# Revit family: VIESSMANN - Vitocal 300-G Pro
name_source: partatom
category: Wyposażenie mechaniczne
revit_build: Autodesk Revit 2017 (Build: 20160720_1515(x64)
units: mm (PartAtom-declared; Revit-internal decimal feet)

## family parameters
Numer OmniClass = 23.75.10.21.17
Oparty na płaszczyźnie roboczej = Nie
Punkt obliczania pomieszczeń = Nie
Tnij formami wycięć po wczytaniu = Nie
Typ części = Normalny
Tytuł OmniClass = Water-Source Heat Pumps
Współdzielony = Nie
Wymiar okrągłego złącza = Użyj średnicy
Zawsze pionowo = Tak

## types (5) — shared parameters
Autor = www.archispace.pl
Czynnik chłodniczy = R410A
Częstotliwość = 50 Hz
Dopuszczalne ciśnienie robocze. Strona niskociśnieniowa = 1.8 MPa
Dopuszczalne ciśnienie robocze. Strona wysokociśnieniowa = 4.5 MPa
Liczba biegunów = 3
Liczba obiegów chłodniczych = 1
Liczba sprężarek = 2
Model = Solankowa pompa ciepła Vitocal 300-G PRO 80kW / Brine-water heat pump Vitocal 300-G PRO 80kW
Napięcie znamionowe = 400 V
Obieg pierwotny od strony parownika (Victaulic) = 3" (DN 80)
Obieg pierwotny od strony zestawu przyłączy (kołnierz) = DN 80/PN 10
Obieg pierwotny. Ochrona przed zamarzaniem/temperatura początku krystalizacji (zalecany czynnik chłodzący Tyfocor) = -16 °C
Obieg pierwotny. Różnica temperatur = 3 °C
Obieg wtórny od strony skraplacza (Victaulic) = 2½" (DN 65)
Obieg wtórny od strony zestawu przyłączy (kołnierz) = DN 65/PN 10
Obieg wtórny. Maks. temperatura na zasilaniu na wlocie z obiegu pierwotnego B +5°C = 60 °C
Obieg wtórny. Maks. temperatura na zasilaniu na wlocie z obiegu pierwotnego B 0°C = 55 °C
Obieg wtórny. Różnica temperatur = 5 °C
Opis = Pompy ciepła z napędem elektrycznym do ogrzewania i podgrzewu ciepłej wody użytkowej w jedno- lub dwusystemowych instalacjach grzewczych.
Podłączenie A odsunięcie = 271 mm  [stored 0.889108 ft]
Podłączenie A wysokość = 1139 mm  [stored 3.73688 ft]
Podłączenie B odsunięcie = 300 mm  [stored 0.984252 ft]
Podłączenie B wysokość = 1169 mm  [stored 3.8353 ft]
Podłączenie C odsunięcie = 271 mm  [stored 0.889108 ft]
Podłączenie C wysokość = 609 mm  [stored 1.99803 ft]
Podłączenie D odsunięcie = 300 mm  [stored 0.984252 ft]
Podłączenie D wysokość = 639 mm  [stored 2.09646 ft]
Producent = Viessmann Sp. z o.o.
Regulator. Bezpiecznik = T6,3AH/250 V
Regulator. Klasa ochrony/stopnień ochrony = IP20
Regulator. Maks. pobór mocy elektrycznej 1. i 2. stopnia = 45 W
Regulator. Maks. pobór mocy elektrycznej 1. stopnia = 25 W
Regulator. Maks. pobór mocy elektrycznej 2. stopnia = 20 W
Regulator. Moc znamionowa = 1000 W
Regulator. Napięcie znamionowe = 1/N/PE 230 V/50 Hz
Regulator. Zabezpieczenie (wewnętrzne) = 1 x B16A
Rodzaj sprężarki = Scroll - całkowicie hermetyczna
Stopień ochrony = IP20
System rozruchowy = Moduł łagodnego rozruchu
Szerokość całkowita = 911 mm  [stored 2.98885 ft]
Szerokość przy wstawianiu bez osłon bocznych = 850 mm  [stored 2.78871 ft]
URL = https://www.viessmann-projektant.pl
Viessmann Kolor 1 = Viessmann Kolor 1
Wysokość całkowita = 1650 mm  [stored 5.41339 ft]
Zasilanie elektryczne (V/ph/Hz) = 3LNPE/400 V/50 Hz
Średnica odejścia 1 = 80 mm  [stored 0.262467 ft]
Średnica odejścia 2 = 65 mm  [stored 0.213255 ft]

## per-type parameters (varying)
- BW 302.D090. Solanka/woda (B0/W35): Całkowity maksymalny pobór mocy=48.0 kW; Całkowity prąd rozruchowy=145 A; Cos Phi sprężarki przy maks. mocy w B20/W35=0.77; Długość całkowita=1383 mm; Ilość oleju=8.5 L; Maks. prąd roboczy=71 A; Masa całkowita (urządzenie podstawowe bez opcjonalnej obudowy)=680.00 kg; Natężenie znamionowe sprężarek (łącznie)=40 A; Obciążenie pozorne=62338 VA; Obieg pierwotny. Dop. ciśnienie robocze=1.0 MPa; Obieg pierwotny. Minimalny przepływ objętościowy=15.4 m³/h; Obieg pierwotny. Opór przepływu przy minimalnym przepływie objętościowym=16.0 kPa; Obieg pierwotny. Opór przepływu przy znamionowym przepływie objętościowym (całkowita strata ciśnienia skraplacza z przyłączami)=29.0 kPa; Obieg pierwotny. Pojemność wymiennika ciepła (solanka)=10.5 L; Obieg pierwotny. Znamionowy przepływ objętościowy (wartość zalecana do projektowania)=20.5 m³/h; Obieg wtórny. Dop. ciśnienie robocze=1.0 MPa; Obieg wtórny. Minimalny przepływ objętościowy=11.0 m³/h; Obieg wtórny. Opór przepływu przy minimalnym przepływie objętościowym=3.0 kPa; Obieg wtórny. Opór przepływu przy znamionowym przepływie objętościowym (całkowita strata ciśnienia skraplacza z przyłączami)=6.0 kPa; Obieg wtórny. Pojemność wymiennika ciepła (woda)=15.2 L; Obieg wtórny. Znamionowy przepływ objętościowy (wartość zalecana do projektowania)=14.7 m³/h; Pobór mocy elektrycznej=18.1 kW; Poziom mocy akustycznej=57 dB(A); Prąd rozruchowy jednej sprężarki=87 A; SCOP LT=4.93; SCOP MT=3.71; Stopień efektywności ε (COP)=4.67; Typ=Vitocal 300-G Pro : BW 302.D090, BW 302.D110; Wielkość napełnienia (wytyczna)=10.50 kg; Współczynnik mocy=0.77; Wydajność chłodnicza=67.6 kW; Zabezpieczenie pompy ciepła=80 A; Znamionowa moc grzewcza=84.8 kW; etas LT=189; etas MT=140
- BW 302.D110. Solanka/woda (B0/W35): Całkowity maksymalny pobór mocy=60.0 kW; Całkowity prąd rozruchowy=177 A; Cos Phi sprężarki przy maks. mocy w B20/W35=0.9; Długość całkowita=1383 mm; Ilość oleju=11.4 L; Maks. prąd roboczy=83 A; Masa całkowita (urządzenie podstawowe bez opcjonalnej obudowy)=860.00 kg; Natężenie znamionowe sprężarek (łącznie)=45 A; Obciążenie pozorne=66667 VA; Obieg pierwotny. Dop. ciśnienie robocze=0.1 MPa; Obieg pierwotny. Minimalny przepływ objętościowy=20.9 m³/h; Obieg pierwotny. Opór przepływu przy minimalnym przepływie objętościowym=19.0 kPa; Obieg pierwotny. Opór przepływu przy znamionowym przepływie objętościowym (całkowita strata ciśnienia skraplacza z przyłączami)=35.0 kPa; Obieg pierwotny. Pojemność wymiennika ciepła (solanka)=10.5 L; Obieg pierwotny. Znamionowy przepływ objętościowy (wartość zalecana do projektowania)=27.9 m³/h; Obieg wtórny. Dop. ciśnienie robocze=0.1 MPa; Obieg wtórny. Minimalny przepływ objętościowy=14.6 m³/h; Obieg wtórny. Opór przepływu przy minimalnym przepływie objętościowym=4.0 kPa; Obieg wtórny. Opór przepływu przy znamionowym przepływie objętościowym (całkowita strata ciśnienia skraplacza z przyłączami)=7.0 kPa; Obieg wtórny. Pojemność wymiennika ciepła (woda)=19.2 L; Obieg wtórny. Znamionowy przepływ objętościowy (wartość zalecana do projektowania)=19.5 m³/h; Pobór mocy elektrycznej=23.5 kW; Poziom mocy akustycznej=63 dB(A); Prąd rozruchowy jednej sprężarki=113 A; SCOP LT=4.85; SCOP MT=3.66; Stopień efektywności ε (COP)=4.61; Typ=Vitocal 300-G Pro : BW 302.D090, BW 302.D110; Wielkość napełnienia (wytyczna)=13.00 kg; Współczynnik mocy=0.9; Wydajność chłodnicza=86.4 kW; Zabezpieczenie pompy ciepła=100 A; Znamionowa moc grzewcza=108.6 kW; etas LT=186; etas MT=138
- BW 302.D140. Solanka/woda (B0/W35): Całkowity maksymalny pobór mocy=73.0 kW; Całkowity prąd rozruchowy=215 A; Cos Phi sprężarki przy maks. mocy w B20/W35=0.89; Długość całkowita=1972 mm  [stored 6.46982 ft]; Ilość oleju=15.6 L; Maks. prąd roboczy=124 A; Masa całkowita (urządzenie podstawowe bez opcjonalnej obudowy)=1150.00 kg; Natężenie znamionowe sprężarek (łącznie)=57 A; Obciążenie pozorne=82022 VA; Obieg pierwotny. Dop. ciśnienie robocze=0.1 MPa; Obieg pierwotny. Minimalny przepływ objętościowy=25.0 m³/h; Obieg pierwotny. Opór przepływu przy minimalnym przepływie objętościowym=17.0 kPa; Obieg pierwotny. Opór przepływu przy znamionowym przepływie objętościowym (całkowita strata ciśnienia skraplacza z przyłączami)=31.0 kPa; Obieg pierwotny. Pojemność wymiennika ciepła (solanka)=17.4 L; Obieg pierwotny. Znamionowy przepływ objętościowy (wartość zalecana do projektowania)=33.3 m³/h; Obieg wtórny. Dop. ciśnienie robocze=0.1 MPa; Obieg wtórny. Minimalny przepływ objętościowy=17.9 m³/h; Obieg wtórny. Opór przepływu przy minimalnym przepływie objętościowym=4.0 kPa; Obieg wtórny. Opór przepływu przy znamionowym przepływie objętościowym (całkowita strata ciśnienia skraplacza z przyłączami)=8.0 kPa; Obieg wtórny. Pojemność wymiennika ciepła (woda)=23.2 L; Obieg wtórny. Znamionowy przepływ objętościowy (wartość zalecana do projektowania)=23.8 m³/h; Pobór mocy elektrycznej=29.7 kW; Poziom mocy akustycznej=66 dB(A); Prąd rozruchowy jednej sprężarki=136 A; SCOP LT=4.89; SCOP MT=3.69; Stopień efektywności ε (COP)=4.63; Typ=Vitocal 300-G Pro : BW 302.D140, BW 302.D180; Wielkość napełnienia (wytyczna)=17.00 kg; Współczynnik mocy=0.89; Wydajność chłodnicza=109.4 kW; Zabezpieczenie pompy ciepła=125 A; Znamionowa moc grzewcza=137.6 kW; etas LT=187; etas MT=140
- BW 302.D180. Solanka/woda (B0/W35): Całkowity maksymalny pobór mocy=48.0 kW; Całkowity prąd rozruchowy=145 A; Cos Phi sprężarki przy maks. mocy w B20/W35=0.77; Długość całkowita=1972 mm  [stored 6.46982 ft]; Ilość oleju=14.6 L; Maks. prąd roboczy=71 A; Masa całkowita (urządzenie podstawowe bez opcjonalnej obudowy)=150.00 kg; Natężenie znamionowe sprężarek (łącznie)=70 A; Obciążenie pozorne=62338 VA; Obieg pierwotny. Dop. ciśnienie robocze=0.1 MPa; Obieg pierwotny. Minimalny przepływ objętościowy=35.4 m³/h; Obieg pierwotny. Opór przepływu przy minimalnym przepływie objętościowym=17.0 kPa; Obieg pierwotny. Opór przepływu przy znamionowym przepływie objętościowym (całkowita strata ciśnienia skraplacza z przyłączami)=31.0 kPa; Obieg pierwotny. Pojemność wymiennika ciepła (solanka)=23.0 L; Obieg pierwotny. Znamionowy przepływ objętościowy (wartość zalecana do projektowania)=47.3 m³/h; Obieg wtórny. Dop. ciśnienie robocze=0.1 MPa; Obieg wtórny. Minimalny przepływ objętościowy=24.3 m³/h; Obieg wtórny. Opór przepływu przy minimalnym przepływie objętościowym=5.0 kPa; Obieg wtórny. Opór przepływu przy znamionowym przepływie objętościowym (całkowita strata ciśnienia skraplacza z przyłączami)=10.0 kPa; Obieg wtórny. Pojemność wymiennika ciepła (woda)=28.3 L; Obieg wtórny. Znamionowy przepływ objętościowy (wartość zalecana do projektowania)=32.4 m³/h; Pobór mocy elektrycznej=37.8 kW; Poziom mocy akustycznej=65 dB(A); Prąd rozruchowy jednej sprężarki=87 A; SCOP LT=4.91; SCOP MT=3.65; Stopień efektywności ε (COP)=4.62; Typ=Vitocal 300-G Pro : BW 302.D140, BW 302.D180; Wielkość napełnienia (wytyczna)=22.00 kg; Współczynnik mocy=0.77; Wydajność chłodnicza=138.8 kW; Zabezpieczenie pompy ciepła=80 A; Znamionowa moc grzewcza=174.8 kW; etas LT=188; etas MT=138
- BW 302.D230. Solanka/woda (B0/W35): Całkowity maksymalny pobór mocy=108.0 kW; Całkowity prąd rozruchowy=312 A; Cos Phi sprężarki przy maks. mocy w B20/W35=0.88; Długość całkowita=1972 mm  [stored 6.46982 ft]; Ilość oleju=14.6 L; Maks. prąd roboczy=182 A; Masa całkowita (urządzenie podstawowe bez opcjonalnej obudowy)=680.00 kg; Natężenie znamionowe sprężarek (łącznie)=86 A; Obciążenie pozorne=122727 VA; Obieg pierwotny. Dop. ciśnienie robocze=0.1 MPa; Obieg pierwotny. Minimalny przepływ objętościowy=40.3 m³/h; Obieg pierwotny. Opór przepływu przy minimalnym przepływie objętościowym=15.0 kPa; Obieg pierwotny. Opór przepływu przy znamionowym przepływie objętościowym (całkowita strata ciśnienia skraplacza z przyłączami)=26.1 kPa; Obieg pierwotny. Pojemność wymiennika ciepła (solanka)=52.4 L; Obieg pierwotny. Znamionowy przepływ objętościowy (wartość zalecana do projektowania)=53.7 m³/h; Obieg wtórny. Dop. ciśnienie robocze=0.1 MPa; Obieg wtórny. Minimalny przepływ objętościowy=28.8 m³/h; Obieg wtórny. Opór przepływu przy minimalnym przepływie objętościowym=6.0 kPa; Obieg wtórny. Opór przepływu przy znamionowym przepływie objętościowym (całkowita strata ciśnienia skraplacza z przyłączami)=10.0 kPa; Obieg wtórny. Pojemność wymiennika ciepła (woda)=53.6 L; Obieg wtórny. Znamionowy przepływ objętościowy (wartość zalecana do projektowania)=38.5 m³/h; Pobór mocy elektrycznej=47.0 kW; Poziom mocy akustycznej=57 dB(A); Prąd rozruchowy jednej sprężarki=204 A; SCOP LT=5.03; SCOP MT=3.77; Stopień efektywności ε (COP)=4.72; Typ=Vitocal 300-G Pro : BW 302.D230; Wielkość napełnienia (wytyczna)=42.30 kg; Współczynnik mocy=0.88; Wydajność chłodnicza=177.4 kW; Zabezpieczenie pompy ciepła=200 A; Znamionowa moc grzewcza=222.0 kW; etas LT=193; etas MT=143

note: [stored X ft] marks values corroborated as IEEE doubles in the binary element streams (Revit-internal decimal feet)

## geometry (parser evidence)
native form markers: Sweep x3
no freeform markers — native parametric forms only
